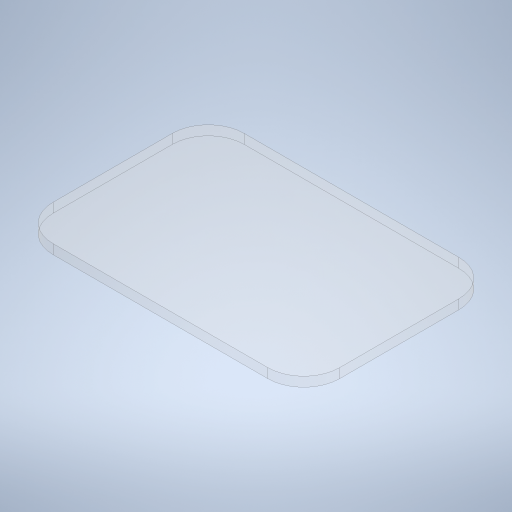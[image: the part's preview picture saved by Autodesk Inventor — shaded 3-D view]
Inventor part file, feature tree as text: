
AUTODESK INVENTOR PART (.ipt)
format: ipt  version: 2024.2 (Build 282272000, 272)  size: 246,784 bytes
history: native  units: in
note: dims shown in document units (in); Inventor stores cm internally (conversion verified against a paired STEP export)
features: extrude x1, sketch x1
ambient origin geometry x8: Origin, YZ Plane, XZ Plane, XY Plane, X Axis, Y Axis, Z Axis, Center Point
bodies: Solid1 (feature_tree)
feature tree (2):
  extrude  "Extrusion1"  Depth=3.0in
  sketch  "Sketch1"  dims[d0=2.0in d1=3.0in d2=0.375in d3=0.375in d4=0.1in d5=0.0in]
